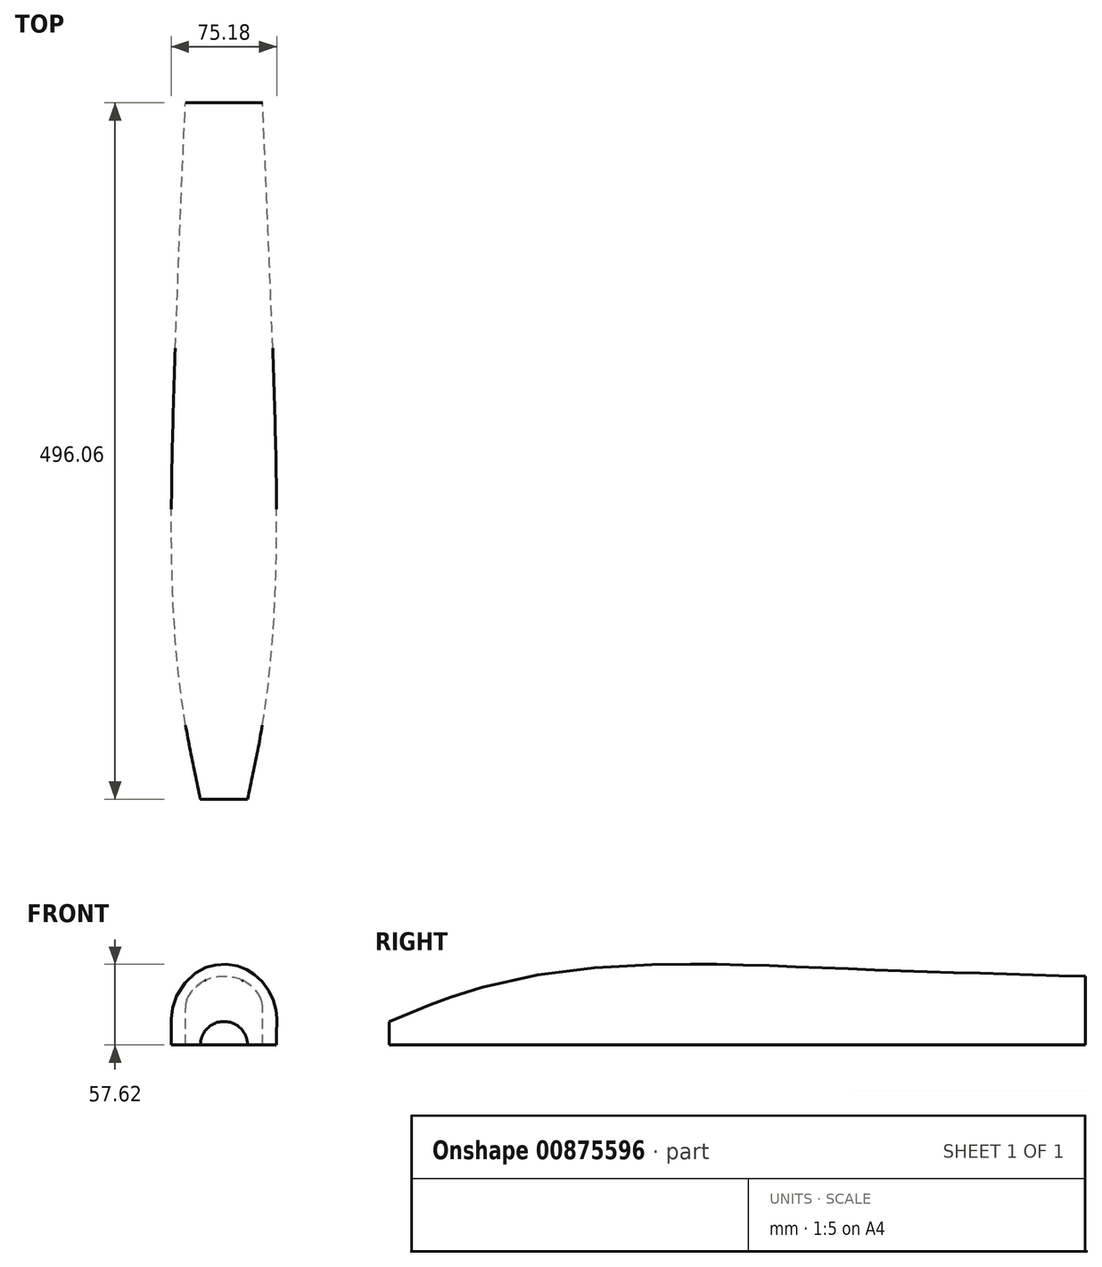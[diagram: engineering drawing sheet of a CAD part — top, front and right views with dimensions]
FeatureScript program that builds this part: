
annotation { "Feature Type Name" : "Feature", "Feature Type Description" : "" }
export const myFeature = defineFeature(function(context is Context, id is Id, definition is map)
    precondition{}
    {
        {
            var Q0;
            Q0=qCreatedBy(makeId("Right.planeOp"),FACE);
            var sketch = newSketch(context, id + "F0", { "sketchPlane" : qUnion([Q0])});
            skLineSegment(sketch, "E0", {"start": v(52.73, -36.3) * mm, "end": v(52.73, 0) * mm});
            skLineSegment(sketch, "E1", {"start": v(206.52, -36.3) * mm, "end": v(206.52, 0) * mm});
            skLineSegment(sketch, "E2", {"start": v(321.16, -36.3) * mm, "end": v(321.16, 0) * mm});
            skLineSegment(sketch, "E3", {"start": v(496.06, -36.3) * mm, "end": v(496.06, 0) * mm});
            skLineSegment(sketch, "E4", {"start": v(572.24, -36.3) * mm, "end": v(572.24, 0) * mm});
            skLineSegment(sketch, "E5", {"start": v(641.02, -36.3) * mm, "end": v(641.02, 0) * mm});
            skLineSegment(sketch, "E6", {"start": v(772.16, -36.3) * mm, "end": v(772.16, 0) * mm});
            skLineSegment(sketch, "E7", {"start": v(0, -36.3) * mm, "end": v(0, 0) * mm});
            skLineSegment(sketch, "E8", {"start": v(0, 0) * mm, "end": v(772.16, 0) * mm});
            skEllipticalArc(sketch, "E9", {});
            skEllipticalArc(sketch, "E10", {});
            skLineSegment(sketch, "E11", {"start": v(80.04, -27.79) * mm, "end": v(80.04, 11.88) * mm});
            skCircle(sketch, "E12", {"center": v(0, 0) * mm, "radius": 16.78 * mm});
            skEllipticalArc(sketch, "E13", {});
            skLineSegment(sketch, "E14", {"start": v(243.94, 16.83) * mm, "end": v(243.94, -41.6) * mm});
            skEllipticalArc(sketch, "E15", {});
            skArc(sketch, "E16", {"start": v(355.83, 10.48) * mm, "mid": v(355.27, 16.29) * mm, "end": v(353.6, 21.88) * mm});
            skLineSegment(sketch, "E17", {"start": v(353.6, 21.88) * mm, "end": v(346.92, 38.2) * mm});
            skLineSegment(sketch, "E18", {"start": v(355.83, 10.48) * mm, "end": v(355.83, -42.01) * mm});
            skEllipticalArc(sketch, "E19", {});
            skEllipticalArc(sketch, "E20", {});
            skLineSegment(sketch, "E21", {"start": v(496.06, -40.78) * mm, "end": v(506.87, -40.14) * mm});
            skLineSegment(sketch, "E22", {"start": v(523.59, -22.4) * mm, "end": v(523.59, 26.07) * mm});
            skArc(sketch, "E23", {"start": v(506.87, -40.14) * mm, "mid": v(518.75, -34.59) * mm, "end": v(523.59, -22.4) * mm});
            skLineSegment(sketch, "E24", {"start": v(520.97, 38.4) * mm, "end": v(512.96, 56.38) * mm});
            skArc(sketch, "E25", {"start": v(513.1, 56.06) * mm, "mid": v(506.25, 64.2) * mm, "end": v(496.06, 67.24) * mm});
            skArc(sketch, "E26", {"start": v(523.59, 26.07) * mm, "mid": v(522.93, 32.37) * mm, "end": v(520.97, 38.4) * mm});
            skLineSegment(sketch, "E27", {"start": v(585.4, 55.62) * mm, "end": v(596.56, 29.66) * mm});
            skArc(sketch, "E28", {"start": v(585.4, 55.62) * mm, "mid": v(579.9, 61.37) * mm, "end": v(572.24, 63.48) * mm});
            skArc(sketch, "E29", {"start": v(581.72, -32.94) * mm, "mid": v(593.14, -28.2) * mm, "end": v(597.87, -16.78) * mm});
            skLineSegment(sketch, "E30", {"start": v(597.87, 23.28) * mm, "end": v(597.87, -16.78) * mm});
            skLineSegment(sketch, "E31", {"start": v(581.72, -32.94) * mm, "end": v(572.24, -32.94) * mm});
            skArc(sketch, "E32", {"start": v(597.87, 23.28) * mm, "mid": v(597.54, 26.54) * mm, "end": v(596.56, 29.66) * mm});
            skArc(sketch, "E33", {"start": v(647.85, -28.87) * mm, "mid": v(656.99, -25.09) * mm, "end": v(660.77, -15.95) * mm});
            skLineSegment(sketch, "E34", {"start": v(647.85, -28.87) * mm, "end": v(641.02, -28.87) * mm});
            skLineSegment(sketch, "E35", {"start": v(659.98, 29.3) * mm, "end": v(654.04, 45.45) * mm});
            skArc(sketch, "E36", {"start": v(654.04, 45.45) * mm, "mid": v(649.31, 51.58) * mm, "end": v(641.91, 53.91) * mm});
            skArc(sketch, "E37", {"start": v(660.77, 24.84) * mm, "mid": v(660.57, 27.1) * mm, "end": v(659.98, 29.3) * mm});
            skLineSegment(sketch, "E38", {"start": v(660.77, -15.95) * mm, "end": v(660.77, 24.84) * mm});
            skLineSegment(sketch, "E39", {"start": v(641.02, 53.91) * mm, "end": v(641.91, 53.91) * mm});
            skLineSegment(sketch, "E40", {"start": v(790.75, 37.77) * mm, "end": v(780.22, 41.57) * mm});
            skLineSegment(sketch, "E41", {"start": v(790.75, 37.77) * mm, "end": v(790.75, 6.71) * mm});
            skArc(sketch, "E42", {"start": v(772.58, -11.46) * mm, "mid": v(785.43, -6.14) * mm, "end": v(790.75, 6.71) * mm});
            skLineSegment(sketch, "E43", {"start": v(780.22, 41.57) * mm, "end": v(780.22, 129.68) * mm});
            skEllipticalArc(sketch, "E44", {});
            skEllipticalArc(sketch, "E45", {});
            skEllipticalArc(sketch, "E46", {});
            skLineSegment(sketch, "E47", {"start": v(25.43, -27.79) * mm, "end": v(25.43, 11.88) * mm});
            skEllipticalArc(sketch, "E48", {});
            skLineSegment(sketch, "E49", {"start": v(169.09, 16.83) * mm, "end": v(169.09, -41.6) * mm});
            skEllipticalArc(sketch, "E50", {});
            skLineSegment(sketch, "E51", {"start": v(559.09, 55.62) * mm, "end": v(547.92, 29.66) * mm});
            skArc(sketch, "E52", {"start": v(572.24, 63.48) * mm, "mid": v(564.58, 61.37) * mm, "end": v(559.09, 55.62) * mm});
            skArc(sketch, "E53", {"start": v(546.61, -16.78) * mm, "mid": v(551.34, -28.2) * mm, "end": v(562.77, -32.94) * mm});
            skLineSegment(sketch, "E54", {"start": v(546.61, 23.28) * mm, "end": v(546.61, -16.78) * mm});
            skLineSegment(sketch, "E55", {"start": v(562.77, -32.94) * mm, "end": v(572.24, -32.94) * mm});
            skArc(sketch, "E56", {"start": v(547.92, 29.66) * mm, "mid": v(546.94, 26.54) * mm, "end": v(546.61, 23.28) * mm});
            skArc(sketch, "E57", {"start": v(621.27, -15.95) * mm, "mid": v(625.06, -25.09) * mm, "end": v(634.2, -28.87) * mm});
            skLineSegment(sketch, "E58", {"start": v(634.2, -28.87) * mm, "end": v(641.02, -28.87) * mm});
            skLineSegment(sketch, "E59", {"start": v(622.07, 29.3) * mm, "end": v(628, 45.45) * mm});
            skArc(sketch, "E60", {"start": v(640.13, 53.91) * mm, "mid": v(632.74, 51.58) * mm, "end": v(628, 45.45) * mm});
            skArc(sketch, "E61", {"start": v(622.07, 29.3) * mm, "mid": v(621.47, 27.1) * mm, "end": v(621.27, 24.84) * mm});
            skLineSegment(sketch, "E62", {"start": v(621.27, -15.95) * mm, "end": v(621.27, 24.84) * mm});
            skLineSegment(sketch, "E63", {"start": v(641.02, 53.91) * mm, "end": v(640.13, 53.91) * mm});
            skArc(sketch, "E64", {"start": v(288.71, 21.88) * mm, "mid": v(287.05, 16.29) * mm, "end": v(286.48, 10.48) * mm});
            skLineSegment(sketch, "E65", {"start": v(288.71, 21.88) * mm, "end": v(295.4, 38.2) * mm});
            skLineSegment(sketch, "E66", {"start": v(286.48, 10.48) * mm, "end": v(286.48, -42.01) * mm});
            skEllipticalArc(sketch, "E67", {});
            skEllipticalArc(sketch, "E68", {});
            skLineSegment(sketch, "E69", {"start": v(496.06, -40.78) * mm, "end": v(485.25, -40.14) * mm});
            skLineSegment(sketch, "E70", {"start": v(468.53, -22.4) * mm, "end": v(468.53, 26.07) * mm});
            skArc(sketch, "E71", {"start": v(468.53, -22.4) * mm, "mid": v(473.37, -34.59) * mm, "end": v(485.25, -40.14) * mm});
            skLineSegment(sketch, "E72", {"start": v(471.15, 38.4) * mm, "end": v(479.16, 56.38) * mm});
            skArc(sketch, "E73", {"start": v(496.06, 67.24) * mm, "mid": v(485.87, 64.2) * mm, "end": v(479.02, 56.06) * mm});
            skArc(sketch, "E74", {"start": v(471.15, 38.4) * mm, "mid": v(469.2, 32.37) * mm, "end": v(468.53, 26.07) * mm});
            skLineSegment(sketch, "E75", {"start": v(772.16, -11.46) * mm, "end": v(772.58, -11.46) * mm});
            skLineSegment(sketch, "E76", {"start": v(753.56, 37.77) * mm, "end": v(764.1, 41.57) * mm});
            skLineSegment(sketch, "E77", {"start": v(753.56, 37.77) * mm, "end": v(753.56, 6.71) * mm});
            skArc(sketch, "E78", {"start": v(753.56, 6.71) * mm, "mid": v(758.88, -6.14) * mm, "end": v(771.73, -11.46) * mm});
            skLineSegment(sketch, "E79", {"start": v(764.1, 41.57) * mm, "end": v(764.1, 129.68) * mm});
            skEllipticalArc(sketch, "E80", {});
            skLineSegment(sketch, "E81", {"start": v(772.16, -11.46) * mm, "end": v(771.73, -11.46) * mm});
            const initialGuessF0  = {"E9": [0.052732863799999974, -0.02778605060000003, 1, 0, 0.027306981200000004, 0.0149469856, 4.71238898038469, 0], "E10": [0.052732863799999974, 0.01188092620000003, 1, 0, 0.027306981200000004, 0.025103277200000003, 0, 1.5707963267948966], "E13": [0.2065151826, 0.016826280799999996, 0, -1, 0.040778430000000004, 0.037427357200000004, 1.570796, 3.141593], "E15": [0.2065151826, -0.041607130400000004, 1, 0, 0.037427357200000004, 0.0172465238, 4.71238898038469, 0], "E19": [0.3211577524, -0.0420116381, -1, 0, 0.03467481000000001, 0.016795445200000002, 1.570796, 3.141592653589793], "E20": [0.3211577524, 0.029726826499999998, 1, 0, 0.0274176998, 0.024822734200000002, 0.348745, 1.5707963267948966], "E44": [0.7721558598, 0.1296840434, 0, 1, 0.024017147800000003, 0.008063611, 4.71238898038469, 0], "E45": [0.052732863799999974, -0.02778605060000003, -1, 0, 0.027306981200000004, 0.0149469856, 0, 1.5707963267948966], "E46": [0.052732863799999974, 0.01188092620000003, -1, 0, 0.027306981200000004, 0.025103277200000003, 4.71238898038469, 0], "E48": [0.2065151826, 0.016826280799999996, 0, -1, 0.040778430000000004, 0.037427357200000004, 3.141592307179583, 4.712389307179587], "E50": [0.2065151826, -0.041607130400000004, -1, 0, 0.037427357200000004, 0.0172465238, 0, 1.5707963267948966], "E67": [0.3211577524, -0.0420116381, 1, 0, 0.03467481000000001, 0.016795445200000002, 3.141592653589793, 4.712389307179588], "E68": [0.3211577524, 0.029726826499999998, -1, 0, 0.0274176998, 0.024822734200000002, 4.71238898038469, 5.934440307179585], "E80": [0.7721558598, 0.1296840434, 0, 1, 0.024017147800000003, 0.008063611, 0, 1.5707963267948966]};
            skSetInitialGuess(sketch, initialGuessF0);
            skSolve(sketch);
        }
        {
            var Q0;
            Q0=qCreatedBy(makeId("Front.planeOp"),FACE);
            var sketch = newSketch(context, id + "F1", { "sketchPlane" : qUnion([Q0])});
            skArc(sketch, "E82", {"start": v(-14.52, 8.38) * mm, "mid": v(0, 16.76) * mm, "end": v(14.52, 8.38) * mm});
            skLineSegment(sketch, "E83", {"start": v(0, 0) * mm, "end": v(0, 16.76) * mm, "construction": true});
            skLineSegment(sketch, "E84.1.0", {"start": v(0, 0) * mm, "end": v(14.52, 8.38) * mm, "construction": true});
            skLineSegment(sketch, "E84.anchor2", {"start": v(0, 0) * mm, "end": v(14.52, 8.38) * mm, "construction": true});
            skLineSegment(sketch, "E85.1.2", {"start": v(0, 0) * mm, "end": v(-14.52, 8.38) * mm, "construction": true});
            skLineSegment(sketch, "E85.1.4", {"start": v(0, 0) * mm, "end": v(-14.52, 8.38) * mm, "construction": true});
            skArc(sketch, "E85.2.1", {"start": v(-16.76, 0) * mm, "mid": v(-16.2, 4.34) * mm, "end": v(-14.52, 8.38) * mm});
            skLineSegment(sketch, "E85.2.3", {"start": v(0, 0) * mm, "end": v(-14.52, 8.38) * mm, "construction": true});
            skLineSegment(sketch, "E85.2.5", {"start": v(0, 0) * mm, "end": v(-14.52, 8.38) * mm, "construction": true});
            skArc(sketch, "E85.5.1", {"start": v(14.52, 8.38) * mm, "mid": v(16.2, 4.34) * mm, "end": v(16.76, 0) * mm});
            skLineSegment(sketch, "E86", {"start": v(-16.76, 0) * mm, "end": v(16.76, 0) * mm});
            skSolve(sketch);
        }
        {
            var Q0;
            Q0=qCreatedBy(makeId("Front.planeOp"),FACE);
            var Q1;
            Q1=sQuery(id+"F0.wireOp",EDGE,"E0");
            cPlane(context, id + "F2", {"entities" : qUnion([Q0, Q1]), "cplaneType" : CPlaneType.LINE_ANGLE, "offset" : 25.4 * mm, "angle" : 0 * degree, "width" : 152.4 * mm, "height" : 152.4 * mm});
        }
        {
            var Q0;
            Q0=qCreatedBy(id+"F2.planeOp",FACE);
            var sketch = newSketch(context, id + "F3", { "sketchPlane" : qUnion([Q0])});
            skLineSegment(sketch, "E87", {"start": v(27.3, 0) * mm, "end": v(27.3, 11.88) * mm});
            skLineSegment(sketch, "E88", {"start": v(-27.3, 0) * mm, "end": v(-27.3, 11.88) * mm});
            skLineSegment(sketch, "E89", {"start": v(27.3, 0) * mm, "end": v(-27.3, 0) * mm});
            skEllipticalArc(sketch, "E90", {});
            skLineSegment(sketch, "E91", {"start": v(0, 0) * mm, "end": v(0, 36.98) * mm, "construction": true});
            const initialGuessF3  = {"E90": [0, 0.01188092620000003, 1, 0, 0.027306993900000014, 0.0251032772, 0, 3.141592653589793]};
            skSetInitialGuess(sketch, initialGuessF3);
            skSolve(sketch);
        }
        {
            var Q0;
            Q0=qCreatedBy(makeId("Front.planeOp"),FACE);
            var Q1;
            Q1=sQuery(id+"F0.wireOp",EDGE,"E1");
            cPlane(context, id + "F4", {"entities" : qUnion([Q0, Q1]), "cplaneType" : CPlaneType.LINE_ANGLE, "offset" : 25.4 * mm, "angle" : 0 * degree, "width" : 152.4 * mm, "height" : 152.4 * mm});
        }
        {
            var Q0;
            Q0=qCreatedBy(id+"F4.planeOp",FACE);
            var sketch = newSketch(context, id + "F5", { "sketchPlane" : qUnion([Q0])});
            skLineSegment(sketch, "E92", {"start": v(37.43, 16.83) * mm, "end": v(37.43, 0) * mm});
            skLineSegment(sketch, "E93", {"start": v(-37.43, 16.83) * mm, "end": v(-37.43, 0) * mm});
            skLineSegment(sketch, "E94", {"start": v(0, 57.6) * mm, "end": v(0, 0) * mm, "construction": true});
            skPoint(sketch, "E95", {"position": v(0, 0) * mm});
            skEllipticalArc(sketch, "E96", {});
            skLineSegment(sketch, "E97", {"start": v(37.43, 0) * mm, "end": v(-37.43, 0) * mm});
            const initialGuessF5  = {"E96": [0, 0.0168262808, 1, 0, 0.03742735719999998, 0.04077843, 6.283185307179586, 3.141592326794896]};
            skSetInitialGuess(sketch, initialGuessF5);
            skSolve(sketch);
        }
        {
            var Q0;
            Q0=qCreatedBy(makeId("Front.planeOp"),FACE);
            var Q1;
            Q1=sQuery(id+"F0.wireOp",EDGE,"E2");
            cPlane(context, id + "F6", {"entities" : qUnion([Q0, Q1]), "cplaneType" : CPlaneType.LINE_ANGLE, "offset" : 25.4 * mm, "angle" : 0 * degree, "width" : 152.4 * mm, "height" : 152.4 * mm});
        }
        {
            var Q0;
            Q0=qCreatedBy(id+"F6.planeOp",FACE);
            var sketch = newSketch(context, id + "F7", { "sketchPlane" : qUnion([Q0])});
            skLineSegment(sketch, "E98", {"start": v(34.67, 0) * mm, "end": v(-34.67, 0) * mm});
            skLineSegment(sketch, "E99", {"start": v(34.67, 10.48) * mm, "end": v(-34.67, 10.48) * mm, "construction": true});
            skEllipticalArc(sketch, "E100", {});
            skLineSegment(sketch, "E101", {"start": v(34.67, 10.48) * mm, "end": v(34.67, 0) * mm});
            skLineSegment(sketch, "E102", {"start": v(-34.67, 10.48) * mm, "end": v(-34.67, 0) * mm});
            skPoint(sketch, "E103", {"position": v(0, 54.55) * mm});
            const initialGuessF7  = {"E100": [0, 0.010476699899999999, 1, 0, 0.03467481000000022, 0.044072844657877926, 6.283185307179586, 3.141592653589793]};
            skSetInitialGuess(sketch, initialGuessF7);
            skSolve(sketch);
        }
        {
            var Q0;
            Q0=qCreatedBy(id+"F6.planeOp",FACE);
            var Q1;
            Q1=sQuery(id+"F0.wireOp",EDGE,"E3");
            cPlane(context, id + "F8", {"entities" : qUnion([Q0, Q1]), "cplaneType" : CPlaneType.LINE_ANGLE, "offset" : 25.4 * mm, "angle" : 0 * degree, "width" : 152.4 * mm, "height" : 152.4 * mm});
        }
        {
            var Q0;
            Q0=qCreatedBy(id+"F8.planeOp",FACE);
            var sketch = newSketch(context, id + "F9", { "sketchPlane" : qUnion([Q0])});
            skLineSegment(sketch, "E104", {"start": v(27.53, -22.4) * mm, "end": v(27.53, 26.07) * mm});
            skArc(sketch, "E105", {"start": v(10.81, -40.14) * mm, "mid": v(22.7, -34.59) * mm, "end": v(27.53, -22.4) * mm});
            skLineSegment(sketch, "E106", {"start": v(24.91, 38.4) * mm, "end": v(16.9, 56.38) * mm});
            skArc(sketch, "E107", {"start": v(27.53, 26.07) * mm, "mid": v(26.87, 32.37) * mm, "end": v(24.91, 38.4) * mm});
            skLineSegment(sketch, "E108", {"start": v(-27.53, -22.4) * mm, "end": v(-27.53, 26.07) * mm});
            skArc(sketch, "E109", {"start": v(-27.53, -22.4) * mm, "mid": v(-22.7, -34.59) * mm, "end": v(-10.81, -40.14) * mm});
            skLineSegment(sketch, "E110", {"start": v(-24.91, 38.4) * mm, "end": v(-16.9, 56.38) * mm});
            skArc(sketch, "E111", {"start": v(-24.91, 38.4) * mm, "mid": v(-26.87, 32.37) * mm, "end": v(-27.53, 26.07) * mm});
            skLineSegment(sketch, "E112", {"start": v(0, -40.14) * mm, "end": v(10.81, -40.14) * mm});
            skArc(sketch, "E113", {"start": v(16.9, 56.38) * mm, "mid": v(0, 67.36) * mm, "end": v(-16.9, 56.38) * mm});
            skLineSegment(sketch, "E114", {"start": v(0, 67.36) * mm, "end": v(0, -40.14) * mm, "construction": true});
            skLineSegment(sketch, "E115", {"start": v(-27.53, 0) * mm, "end": v(0, 0) * mm, "construction": true});
            skLineSegment(sketch, "E116.MirrorCS", {"start": v(0, -40.14) * mm, "end": v(-10.81, -40.14) * mm});
            skSolve(sketch);
        }
        {
            var Q0;
            Q0=qCreatedBy(id+"F8.planeOp",FACE);
            var sketch = newSketch(context, id + "F10", { "sketchPlane" : qUnion([Q0])});
            skLineSegment(sketch, "E117", {"start": v(27.53, 0) * mm, "end": v(27.53, 26.07) * mm});
            skLineSegment(sketch, "E118", {"start": v(-27.53, 0) * mm, "end": v(-27.53, 26.07) * mm});
            skLineSegment(sketch, "E119", {"start": v(0, 67.36) * mm, "end": v(0, 0) * mm, "construction": true});
            skLineSegment(sketch, "E120", {"start": v(-27.53, 0) * mm, "end": v(27.53, 0) * mm});
            skLineSegment(sketch, "E121", {"start": v(-27.53, 26.07) * mm, "end": v(27.53, 26.07) * mm, "construction": true});
            skEllipticalArc(sketch, "E122", {});
            const initialGuessF10  = {"E122": [0, 0.026067410399999984, -1, 0, 0.027530526599999994, 0.02279078646298084, 3.141592653589793, 0]};
            skSetInitialGuess(sketch, initialGuessF10);
            skSolve(sketch);
        }
        {
            var Q0;
            Q0=qCreatedBy(id+"F8.planeOp",FACE);
            var Q1;
            Q1=sQuery(id+"F0.wireOp",EDGE,"E4");
            cPlane(context, id + "F11", {"entities" : qUnion([Q0, Q1]), "cplaneType" : CPlaneType.LINE_ANGLE, "offset" : 25.4 * mm, "angle" : 0 * degree, "width" : 152.4 * mm, "height" : 152.4 * mm});
        }
        {
            var Q0;
            Q0=qCreatedBy(makeId("Front.planeOp"),FACE);
            var Q1;
            Q1=sQuery(id+"F0.wireOp",EDGE,"E5");
            cPlane(context, id + "F12", {"entities" : qUnion([Q0, Q1]), "cplaneType" : CPlaneType.LINE_ANGLE, "offset" : 25.4 * mm, "angle" : 0 * degree, "width" : 152.4 * mm, "height" : 152.4 * mm});
        }
        {
            var Q0;
            Q0=qCreatedBy(makeId("Front.planeOp"),FACE);
            var Q1;
            Q1=sQuery(id+"F0.wireOp",EDGE,"E6");
            cPlane(context, id + "F13", {"entities" : qUnion([Q0, Q1]), "cplaneType" : CPlaneType.LINE_ANGLE, "offset" : 25.4 * mm, "angle" : 0 * degree, "width" : 152.4 * mm, "height" : 152.4 * mm});
        }
        {
            var Q0;
            Q0=qSketchRegion(id+"F1",true);
            var Q1;
            Q1=qSketchRegion(id+"F3",true);
            var Q2;
            Q2=qSketchRegion(id+"F5",true);
            var Q3;
            Q3=qSketchRegion(id+"F7",true);
            var Q4;
            Q4=qSketchRegion(id+"F10",true);
            loft(context, id + "F14", {"sheetProfilesArray" : [{ "sheetProfileEntities" : qUnion([Q0]) }, { "sheetProfileEntities" : qUnion([Q1]) }, { "sheetProfileEntities" : qUnion([Q2]) }, { "sheetProfileEntities" : qUnion([Q3]) }, { "sheetProfileEntities" : qUnion([Q4]) }]});
        }
    });
